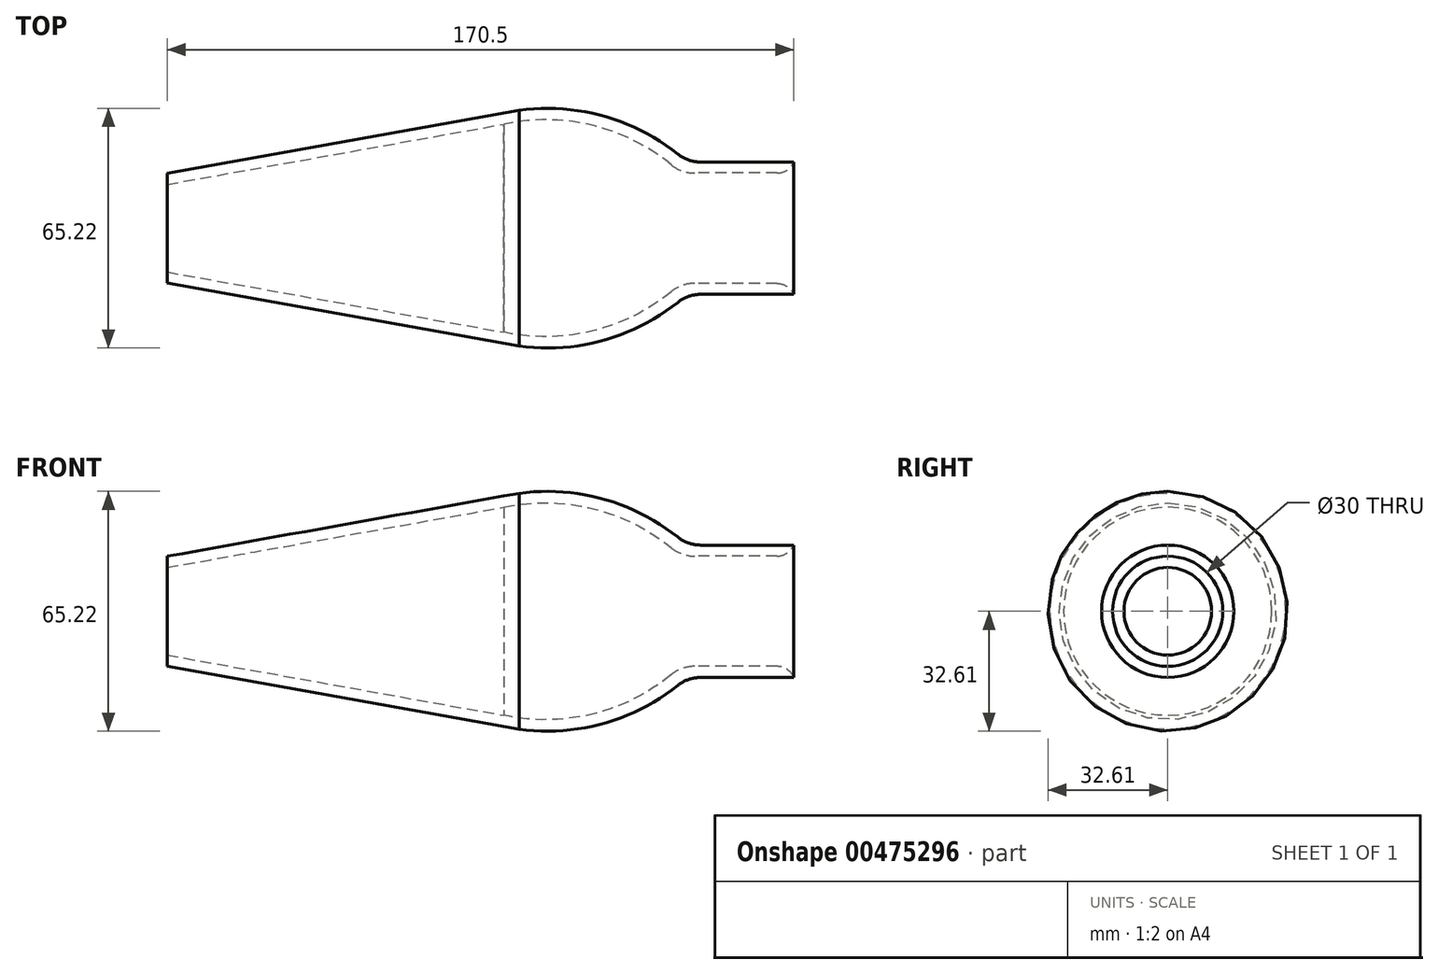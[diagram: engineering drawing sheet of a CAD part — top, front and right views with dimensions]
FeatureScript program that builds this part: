
annotation { "Feature Type Name" : "Feature", "Feature Type Description" : "" }
export const myFeature = defineFeature(function(context is Context, id is Id, definition is map)
    precondition{}
    {
        {
            var Q0;
            Q0=qCreatedBy(makeId("Front.planeOp"),FACE);
            var sketch = newSketch(context, id + "F0", { "sketchPlane" : qUnion([Q0])});
            skPoint(sketch, "E0.start.orphan", {"position": v(-58.28, 0) * mm});
            skLineSegment(sketch, "E1", {"start": v(-98.06, 11.92) * mm, "end": v(-98.06, 14.96) * mm});
            skLineSegment(sketch, "E2", {"start": v(-98.06, 14.96) * mm, "end": v(-2.33, 32.1) * mm});
            skLineSegment(sketch, "E3", {"start": v(43.44, 18) * mm, "end": v(72.44, 18) * mm});
            skLineSegment(sketch, "E4", {"start": v(-98.06, 11.92) * mm, "end": v(-2.77, 28.97) * mm});
            skLineSegment(sketch, "E5", {"start": v(41.67, 15) * mm, "end": v(72.44, 15) * mm});
            skLineSegment(sketch, "E6", {"start": v(72.44, 15) * mm, "end": v(72.44, 18) * mm});
            skPoint(sketch, "E7.orphan", {"position": v(-98.06, 0) * mm});
            skLineSegment(sketch, "E8", {"start": v(-98.06, 0) * mm, "end": v(100.1, 0) * mm});
            skLineSegment(sketch, "E9.MirrorCS", {"start": v(72.44, -15) * mm, "end": v(72.44, -18) * mm});
            skLineSegment(sketch, "E10.MirrorCS", {"start": v(-98.06, -11.92) * mm, "end": v(-98.06, -14.96) * mm});
            skPoint(sketch, "E11.MirrorCS.end.orphan", {"position": v(21.86, -33.37) * mm});
            skPoint(sketch, "E11.MirrorCS.start.orphan", {"position": v(-98.06, -11.92) * mm});
            skPoint(sketch, "E12.MirrorCS.end.orphan", {"position": v(21.94, -36.44) * mm});
            skPoint(sketch, "E12.MirrorCS.start.orphan", {"position": v(-98.06, -14.96) * mm});
            skPoint(sketch, "E13.MirrorCS.end.orphan", {"position": v(41.85, -18) * mm});
            skPoint(sketch, "E14.MirrorCS.end.orphan", {"position": v(41.67, -15) * mm});
            skPoint(sketch, "E15.MirrorCS.end.orphan", {"position": v(72.44, -18) * mm});
            skPoint(sketch, "E16.MirrorCS.end.orphan", {"position": v(72.44, -15) * mm});
            skArc(sketch, "E17", {"start": v(41.67, 15) * mm, "mid": v(19.22, 27.56) * mm, "end": v(-6.5, 28.3) * mm});
            skArc(sketch, "E18", {"start": v(43.44, 18) * mm, "mid": v(19.82, 30.74) * mm, "end": v(-7, 31.26) * mm});
            skPoint(sketch, "E19.orphan", {"position": v(21.94, 36.44) * mm});
            skPoint(sketch, "E20.orphan", {"position": v(21.86, 33.37) * mm});
            skPoint(sketch, "E21.orphan", {"position": v(41.85, 18) * mm});
            skSolve(sketch);
        }
        {
            var Q0;
            Q0=makeQuery(id+"F0.imprint","IMPRINT",FACE,{"disambiguationData":[TD([[makeQuery(id+"F0.imprint","IMPRINT",EDGE,{"derivedFrom":sQuery(id+"F0.wireOp",EDGE,"E1")}),-1.0]])]});
            var Q1;
            Q1=sQuery(id+"F0.wireOp",EDGE,"E8");
            revolve(context, id + "F1", {"entities" : qUnion([Q0]), "axis" : qUnion([Q1]), "revolveType" : RevolveType.FULL});
        }
        {
            var Q0;
            Q0=makeQuery(id+"F1.opRevolve","SWEPT_EDGE",EDGE,{"disambiguationData":[OSD([sQuery(id+"F0.wireOp",EDGE,"E3"),sQuery(id+"F0.wireOp",EDGE,"E18")])]});
            fillet(context, id + "F2", {"entities" : qUnion([Q0]), "radius" : 10 * mm, "tangentPropagation" : true, "allowEdgeOverflow" : false});
        }
        {
            var Q0;
            Q0=makeQuery(id+"F1.opRevolve","SWEPT_EDGE",EDGE,{"disambiguationData":[OSD([sQuery(id+"F0.wireOp",EDGE,"E5"),sQuery(id+"F0.wireOp",EDGE,"E6")])]});
            fillet(context, id + "F3", {"entities" : qUnion([Q0]), "radius" : 5 * mm, "tangentPropagation" : true, "allowEdgeOverflow" : false});
        }
        {
            var Q0;
            Q0=makeQuery(id+"F1.opRevolve","SWEPT_EDGE",EDGE,{"disambiguationData":[OSD([sQuery(id+"F0.wireOp",EDGE,"E5"),sQuery(id+"F0.wireOp",EDGE,"E17")])]});
            fillet(context, id + "F4", {"entities" : qUnion([Q0]), "radius" : 10 * mm, "tangentPropagation" : true, "allowEdgeOverflow" : false});
        }
    });
